# Revit family: Shower_System-GROHE-Euphoria-26490_Series
name_source: partatom
category: Plumbing Fixtures
units: mm (PartAtom-declared; Revit-internal decimal feet)

## family parameters
Cut with Voids When Loaded = No
Host = Face
OmniClass Number = 23.45.05.14.17
OmniClass Title = Showers
Part Type = Normal
Room Calculation Point = No
Round Connector Dimension = Use Diameter
Shared = Yes

## types (2) — shared parameters
ADA Compliant = Yes
Assembly Code = D2010710
CW Connection = Yes
CWFU = 3
Cold Water Connection Diameter = 1/2"
Cold Water Connection Radius = 1/4"
Default Elevation = 78"
Description = Euphoria System Shower system with bath thermostat for wall mounting
EPA WaterSense® Certified = Yes
Flow Rate = 5.3 gpm (20 L/min) at 45 PSI
HW Connection = Yes
HWFU = 3
Height = 62 9/16"
Hot Water Connection Diameter = 1"
Hot Water Connection Radius = 1/4"
IAPMO Compliance = Applicable Codes & Standards - ASME A112.18.1/CSA B125.1 and US Federal and State material regulations and ICC/ANSI A117.1
Inlet Width = 5 7/8"
Inlet Width Constraint = 5 7/8"
Installation Type = Wall Mounted
Length = 18 11/16"
Manufacturer = Grohe
Price = Prices may vary. Please consult Manufacturer Representative for most up-to-date price list.
Product Documentation Link = https://americanstandard.box.com
Product Page URL = https://www.grohe.us
Revised Date = 04/26/2022
Tempered Connection Diameter = 1/2"
Tempered Connection Radius = 1/4"
URL = https://www.grohe.us
Vent Connection = No
WFU = 4
Warranty Documentation Link = https://cdn.cloud.grohe.com
Waste Connection = No
Width = 11 3/4"
cUPC Compliant = Yes

## per-type parameters (varying)
| type | Finish | Material | Min. recommended pressure |
| 26490000 | Metal-Grohe-000-Chrome | Metal-Grohe-000-Chrome | 15 psi (1.0 bar) |
| 26490EN0 | Metal-Grohe-EN0-Brushed Nickel | Metal-Grohe-EN0-Brushed Nickel | 15 psi (1.0 bar |

note: column(s) folded — value = type name in every type: Model

## geometry (parser evidence)
native form markers: Sweep x2
no freeform markers — native parametric forms only
